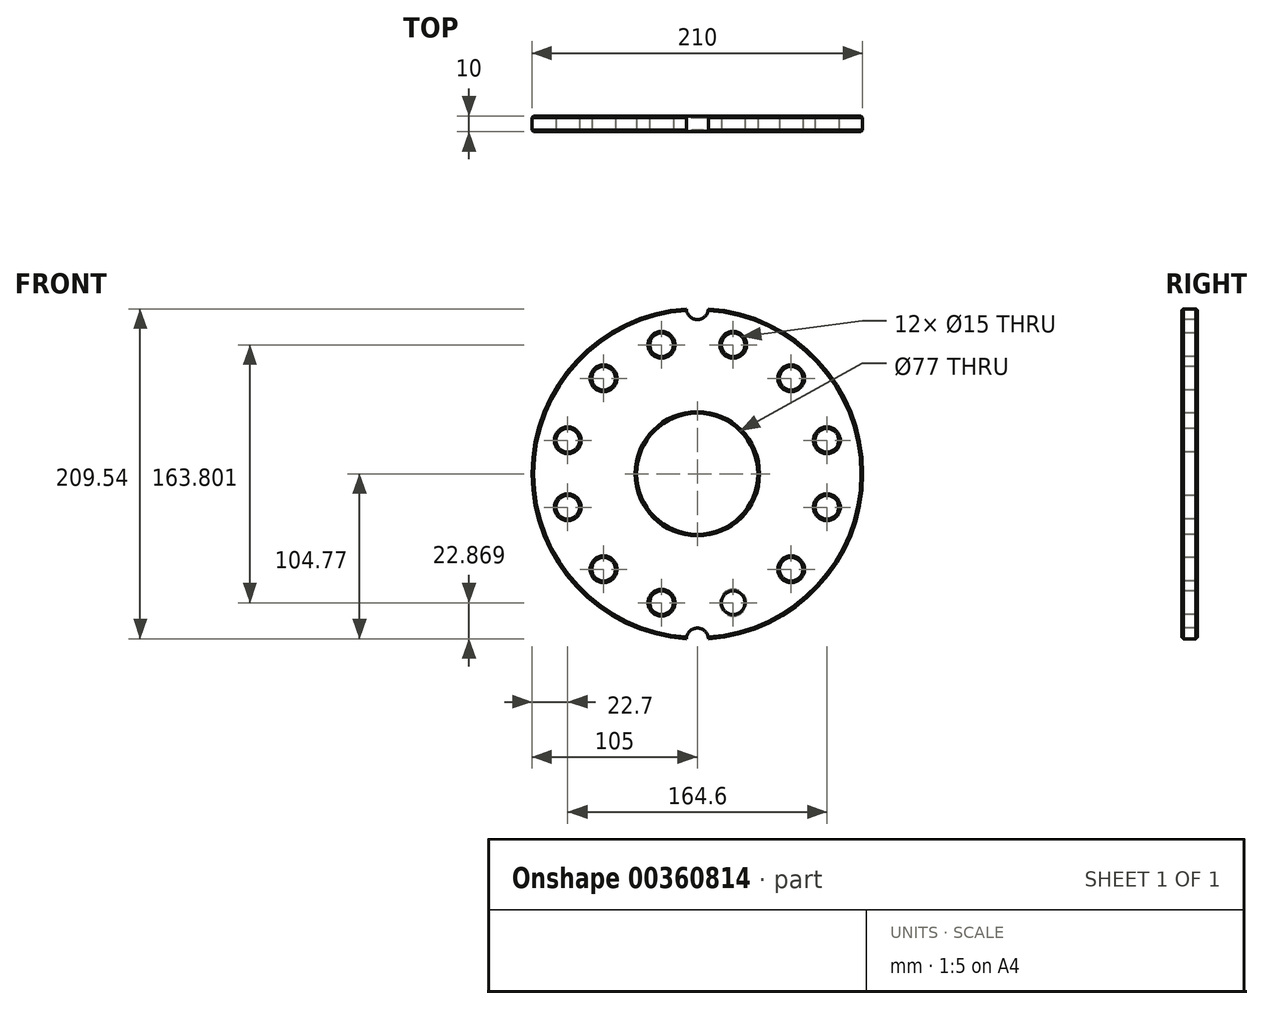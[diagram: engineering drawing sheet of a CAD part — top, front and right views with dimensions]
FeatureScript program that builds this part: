
annotation { "Feature Type Name" : "Feature", "Feature Type Description" : "" }
export const myFeature = defineFeature(function(context is Context, id is Id, definition is map)
    precondition{}
    {
        {
            var Q0;
            Q0=qCreatedBy(makeId("Front.planeOp"),FACE);
            var sketch = newSketch(context, id + "F0", { "sketchPlane" : qUnion([Q0])});
            skCircle(sketch, "E0", {"center": v(0, 0) * mm, "radius": 38.5 * mm});
            skArc(sketch, "E1", {"start": v(-7, 104.77) * mm, "mid": v(-105, 0) * mm, "end": v(-7, -104.77) * mm});
            skLineSegment(sketch, "E2", {"start": v(-105, 0) * mm, "end": v(105, 0) * mm});
            skLineSegment(sketch, "E3", {"start": v(0, -98) * mm, "end": v(0, 98) * mm});
            skArc(sketch, "E4", {"start": v(-7, 104.77) * mm, "mid": v(0, 98) * mm, "end": v(7, 104.77) * mm});
            skArc(sketch, "E5", {"start": v(7, -104.77) * mm, "mid": v(0, -98) * mm, "end": v(-7, -104.77) * mm});
            skArc(sketch, "E6.trimOffspring", {"start": v(7, -104.77) * mm, "mid": v(105, 0) * mm, "end": v(7, 104.77) * mm});
            skLineSegment(sketch, "E7", {"start": v(0, 0) * mm, "end": v(22.74, 81.9) * mm});
            skLineSegment(sketch, "E8", {"start": v(0, 0) * mm, "end": v(-22.74, 81.9) * mm});
            skCircle(sketch, "E9", {"center": v(-22.74, 81.9) * mm, "radius": 7.5 * mm});
            skCircle(sketch, "E10", {"center": v(22.74, 81.9) * mm, "radius": 7.5 * mm});
            skCircle(sketch, "E11.1.0", {"center": v(-82.3, 21.25) * mm, "radius": 7.5 * mm});
            skCircle(sketch, "E11.2.0", {"center": v(-59.56, -60.65) * mm, "radius": 7.5 * mm});
            skCircle(sketch, "E12.1.3.0", {"center": v(22.74, -81.9) * mm, "radius": 7.5 * mm});
            skCircle(sketch, "E12.1.4.0", {"center": v(82.3, -21.25) * mm, "radius": 7.5 * mm});
            skCircle(sketch, "E12.1.5.0", {"center": v(59.56, 60.65) * mm, "radius": 7.5 * mm});
            skCircle(sketch, "E13.1.0", {"center": v(-59.56, 60.65) * mm, "radius": 7.5 * mm});
            skCircle(sketch, "E13.2.0", {"center": v(-82.3, -21.25) * mm, "radius": 7.5 * mm});
            skCircle(sketch, "E13.3.0", {"center": v(-22.74, -81.9) * mm, "radius": 7.5 * mm});
            skCircle(sketch, "E13.4.0", {"center": v(59.56, -60.65) * mm, "radius": 7.5 * mm});
            skCircle(sketch, "E13.5.0", {"center": v(82.3, 21.25) * mm, "radius": 7.5 * mm});
            skSolve(sketch);
        }
        {
            var Q0;
            Q0 = qSketchRegion(id + "F0", true);
            extrude(context, id + "F1", {"entities" : qUnion([Q0]), "oppositeDirection" : true, "depth" : 10 * mm});
        }
        {
            var Q0;
            Q0=makeQuery(id+"F1.opExtrude","CAP_EDGE",EDGE,{"disambiguationData":[OSD([sQuery(id+"F0.wireOp",EDGE,"E0")])],"isStart":true});
            var Q1;
            Q1=makeQuery(id+"F1.opExtrude","CAP_EDGE",EDGE,{"disambiguationData":[OSD([sQuery(id+"F0.wireOp",EDGE,"E6.trimOffspring")])],"isStart":true});
            var Q2;
            Q2=makeQuery(id+"F1.opExtrude","CAP_EDGE",EDGE,{"disambiguationData":[OSD([sQuery(id+"F0.wireOp",EDGE,"E1")])],"isStart":true});
            var Q3;
            Q3=makeQuery(id+"F1.opExtrude","CAP_EDGE",EDGE,{"disambiguationData":[OSD([sQuery(id+"F0.wireOp",EDGE,"E11.1.0")])],"isStart":true});
            var Q4;
            Q4=makeQuery(id+"F1.opExtrude","CAP_EDGE",EDGE,{"disambiguationData":[OSD([sQuery(id+"F0.wireOp",EDGE,"E13.1.0")])],"isStart":true});
            var Q5;
            Q5=makeQuery(id+"F1.opExtrude","CAP_EDGE",EDGE,{"disambiguationData":[OSD([sQuery(id+"F0.wireOp",EDGE,"E9")])],"isStart":true});
            var Q6;
            Q6=makeQuery(id+"F1.opExtrude","CAP_EDGE",EDGE,{"disambiguationData":[OSD([sQuery(id+"F0.wireOp",EDGE,"E10")])],"isStart":true});
            var Q7;
            Q7=makeQuery(id+"F1.opExtrude","CAP_EDGE",EDGE,{"disambiguationData":[OSD([sQuery(id+"F0.wireOp",EDGE,"E12.1.5.0")])],"isStart":true});
            var Q8;
            Q8=makeQuery(id+"F1.opExtrude","CAP_EDGE",EDGE,{"disambiguationData":[OSD([sQuery(id+"F0.wireOp",EDGE,"E13.5.0")])],"isStart":true});
            var Q9;
            Q9=makeQuery(id+"F1.opExtrude","CAP_EDGE",EDGE,{"disambiguationData":[OSD([sQuery(id+"F0.wireOp",EDGE,"E12.1.4.0")])],"isStart":true});
            var Q10;
            Q10=makeQuery(id+"F1.opExtrude","CAP_EDGE",EDGE,{"disambiguationData":[OSD([sQuery(id+"F0.wireOp",EDGE,"E13.4.0")])],"isStart":true});
            var Q11;
            Q11=makeQuery(id+"F1.opExtrude","CAP_EDGE",EDGE,{"disambiguationData":[OSD([sQuery(id+"F0.wireOp",EDGE,"E12.1.3.0")])],"isStart":false});
            var Q12;
            Q12=makeQuery(id+"F1.opExtrude","CAP_EDGE",EDGE,{"disambiguationData":[OSD([sQuery(id+"F0.wireOp",EDGE,"E13.3.0")])],"isStart":true});
            var Q13;
            Q13=makeQuery(id+"F1.opExtrude","CAP_EDGE",EDGE,{"disambiguationData":[OSD([sQuery(id+"F0.wireOp",EDGE,"E11.2.0")])],"isStart":true});
            var Q14;
            Q14=makeQuery(id+"F1.opExtrude","CAP_EDGE",EDGE,{"disambiguationData":[OSD([sQuery(id+"F0.wireOp",EDGE,"E13.2.0")])],"isStart":true});
            chamfer(context, id + "F2", {"entities" : qUnion([Q0, Q1, Q2, Q3, Q4, Q5, Q6, Q7, Q8, Q9, Q10, Q11, Q12, Q13, Q14]), "chamferType" : ChamferType.OFFSET_ANGLE, "width" : 1 * mm, "oppositeDirection" : false, "angle" : 45 * degree, "tangentPropagation" : true});
        }
        {
            var Q0;
            Q0=makeQuery(id+"F1.opExtrude","CAP_EDGE",EDGE,{"disambiguationData":[OSD([sQuery(id+"F0.wireOp",EDGE,"E0")])],"isStart":false});
            var Q1;
            {var subQ0=sQuery(id+"F0.wireOp",EDGE,"E9");Q1=makeQuery(id+"F2.opChamfer","BLEND_EDGE",EDGE,{"blendedFrom":[makeQuery(id+"F1.opExtrude","CAP_EDGE",EDGE,{"disambiguationData":[OSD([subQ0])],"isStart":true}),makeQuery(id+"F1.opExtrude","SWEPT_FACE",FACE,{"disambiguationData":[OSD([subQ0])]})],"blendedInto":[makeQuery(id+"F1.opExtrude","SWEPT_FACE",FACE,{"disambiguationData":[OSD([subQ0])]})]});}
            var Q2;
            Q2=makeQuery(id+"F1.opExtrude","CAP_EDGE",EDGE,{"disambiguationData":[OSD([sQuery(id+"F0.wireOp",EDGE,"E13.1.0")])],"isStart":false});
            var Q3;
            Q3=makeQuery(id+"F1.opExtrude","CAP_EDGE",EDGE,{"disambiguationData":[OSD([sQuery(id+"F0.wireOp",EDGE,"E11.1.0")])],"isStart":false});
            var Q4;
            Q4=makeQuery(id+"F1.opExtrude","CAP_EDGE",EDGE,{"disambiguationData":[OSD([sQuery(id+"F0.wireOp",EDGE,"E13.2.0")])],"isStart":false});
            var Q5;
            Q5=makeQuery(id+"F1.opExtrude","CAP_EDGE",EDGE,{"disambiguationData":[OSD([sQuery(id+"F0.wireOp",EDGE,"E11.2.0")])],"isStart":false});
            var Q6;
            {var subQ0=sQuery(id+"F0.wireOp",EDGE,"E12.1.3.0");Q6=makeQuery(id+"F2.opChamfer","BLEND_EDGE",EDGE,{"blendedFrom":[makeQuery(id+"F1.opExtrude","CAP_EDGE",EDGE,{"disambiguationData":[OSD([subQ0])],"isStart":false}),makeQuery(id+"F1.opExtrude","SWEPT_FACE",FACE,{"disambiguationData":[OSD([subQ0])]})],"blendedInto":[makeQuery(id+"F1.opExtrude","SWEPT_FACE",FACE,{"disambiguationData":[OSD([subQ0])]})]});}
            var Q7;
            Q7=makeQuery(id+"F1.opExtrude","CAP_EDGE",EDGE,{"disambiguationData":[OSD([sQuery(id+"F0.wireOp",EDGE,"E13.3.0")])],"isStart":false});
            var Q8;
            Q8=makeQuery(id+"F1.opExtrude","CAP_EDGE",EDGE,{"disambiguationData":[OSD([sQuery(id+"F0.wireOp",EDGE,"E13.4.0")])],"isStart":false});
            var Q9;
            Q9=makeQuery(id+"F1.opExtrude","CAP_EDGE",EDGE,{"disambiguationData":[OSD([sQuery(id+"F0.wireOp",EDGE,"E12.1.4.0")])],"isStart":false});
            var Q10;
            Q10=makeQuery(id+"F1.opExtrude","CAP_EDGE",EDGE,{"disambiguationData":[OSD([sQuery(id+"F0.wireOp",EDGE,"E13.5.0")])],"isStart":false});
            var Q11;
            Q11=makeQuery(id+"F1.opExtrude","CAP_EDGE",EDGE,{"disambiguationData":[OSD([sQuery(id+"F0.wireOp",EDGE,"E12.1.5.0")])],"isStart":false});
            var Q12;
            Q12=makeQuery(id+"F1.opExtrude","CAP_EDGE",EDGE,{"disambiguationData":[OSD([sQuery(id+"F0.wireOp",EDGE,"E10")])],"isStart":false});
            chamfer(context, id + "F3", {"entities" : qUnion([Q0, Q1, Q2, Q3, Q4, Q5, Q6, Q7, Q8, Q9, Q10, Q11, Q12]), "chamferType" : ChamferType.OFFSET_ANGLE, "width" : 1 * mm, "oppositeDirection" : false, "angle" : 45 * degree, "tangentPropagation" : true});
        }
        {
            var Q0;
            Q0=makeQuery(id+"F1.opExtrude","CAP_EDGE",EDGE,{"disambiguationData":[OSD([sQuery(id+"F0.wireOp",EDGE,"E9")])],"isStart":false});
            var Q1;
            Q1=makeQuery(id+"F1.opExtrude","CAP_EDGE",EDGE,{"disambiguationData":[OSD([sQuery(id+"F0.wireOp",EDGE,"E6.trimOffspring")])],"isStart":false});
            var Q2;
            Q2=makeQuery(id+"F1.opExtrude","CAP_EDGE",EDGE,{"disambiguationData":[OSD([sQuery(id+"F0.wireOp",EDGE,"E1")])],"isStart":false});
            chamfer(context, id + "F4", {"entities" : qUnion([Q0, Q1, Q2]), "chamferType" : ChamferType.OFFSET_ANGLE, "width" : 1 * mm, "oppositeDirection" : false, "angle" : 45 * degree, "tangentPropagation" : true});
        }
    });
